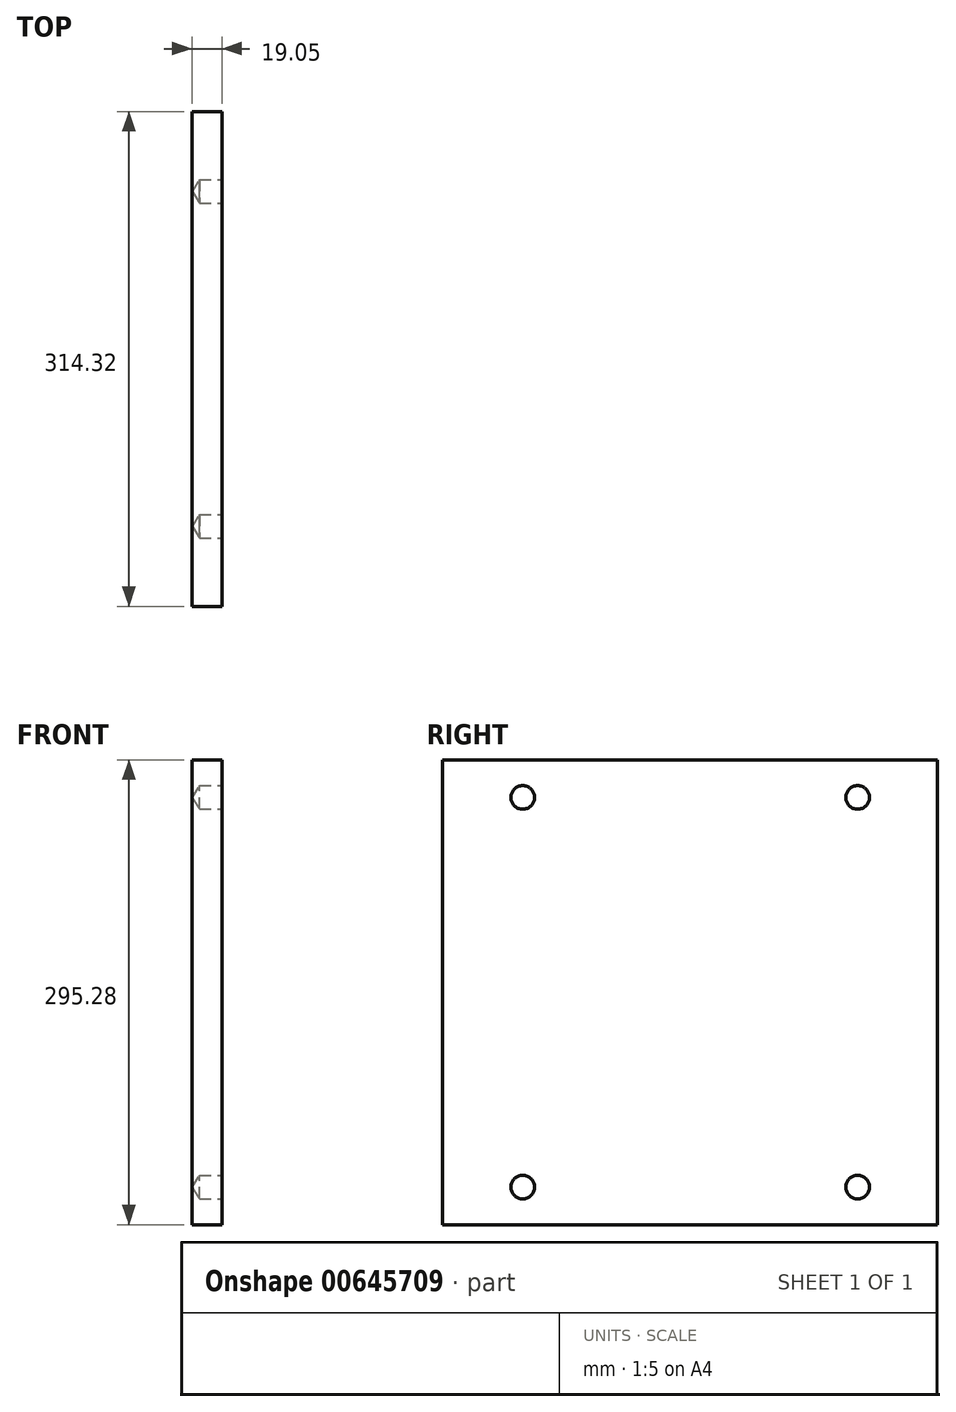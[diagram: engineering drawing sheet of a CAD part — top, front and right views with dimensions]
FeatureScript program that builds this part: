
annotation { "Feature Type Name" : "Feature", "Feature Type Description" : "" }
export const myFeature = defineFeature(function(context is Context, id is Id, definition is map)
    precondition{}
    {
        {
            var Q0;
            Q0=qCreatedBy(makeId("Right.planeOp"),FACE);
            var sketch = newSketch(context, id + "F0", { "sketchPlane" : qUnion([Q0])});
            skLineSegment(sketch, "E0.bottom", {"start": v(157.16, 147.64) * mm, "end": v(-157.16, 147.64) * mm});
            skLineSegment(sketch, "E0.top", {"start": v(157.16, -147.64) * mm, "end": v(-157.16, -147.64) * mm});
            skLineSegment(sketch, "E0.left", {"start": v(157.16, 147.64) * mm, "end": v(157.16, -147.64) * mm});
            skLineSegment(sketch, "E0.right", {"start": v(-157.16, 147.64) * mm, "end": v(-157.16, -147.64) * mm});
            skPoint(sketch, "E0.middle", {"position": v(0, 0) * mm});
            skSolve(sketch);
        }
        {
            var Q0;
            Q0=makeQuery(id+"F0.imprint","IMPRINT",FACE,{"disambiguationData":[TD([[makeQuery(id+"F0.imprint","IMPRINT",EDGE,{"derivedFrom":sQuery(id+"F0.wireOp",EDGE,"E0.bottom")}),1.0]])]});
            extrude(context, id + "F1", {"entities" : qUnion([Q0]), "depth" : 19.05 * mm, "offsetDistance" : 25.4 * mm});
        }
        {
            var Q0;
            Q0=makeQuery(id+"F1.opExtrude","CAP_FACE",FACE,{"disambiguationData":[OSD([sQuery(id+"F0.wireOp",EDGE,"E0.bottom"),sQuery(id+"F0.wireOp",EDGE,"E0.top"),sQuery(id+"F0.wireOp",EDGE,"E0.left"),sQuery(id+"F0.wireOp",EDGE,"E0.right")])],"isStart":false});
            var sketch = newSketch(context, id + "F2", { "sketchPlane" : qUnion([Q0])});
            skLineSegment(sketch, "E1", {"start": v(-157.16, 147.64) * mm, "end": v(-106.36, 147.64) * mm});
            skLineSegment(sketch, "E2", {"start": v(-106.36, 147.64) * mm, "end": v(-106.36, 123.76) * mm});
            skLineSegment(sketch, "E3", {"start": v(157.16, 147.64) * mm, "end": v(106.36, 147.64) * mm});
            skLineSegment(sketch, "E4", {"start": v(106.36, 147.64) * mm, "end": v(106.36, 123.76) * mm});
            skPoint(sketch, "E5", {"position": v(-106.36, 123.76) * mm});
            skPoint(sketch, "E6", {"position": v(106.36, 123.76) * mm});
            skLineSegment(sketch, "E7", {"start": v(-157.16, -147.64) * mm, "end": v(-106.36, -147.64) * mm});
            skLineSegment(sketch, "E8", {"start": v(-106.36, -147.64) * mm, "end": v(-106.36, -123.76) * mm});
            skLineSegment(sketch, "E9", {"start": v(157.16, -147.64) * mm, "end": v(106.36, -147.64) * mm});
            skLineSegment(sketch, "E10", {"start": v(106.36, -147.64) * mm, "end": v(106.36, -123.76) * mm});
            skPoint(sketch, "E11", {"position": v(-106.36, -123.76) * mm});
            skPoint(sketch, "E12", {"position": v(106.36, -123.76) * mm});
            skSolve(sketch);
        }
        {
            var Q0;
            Q0=sQuery(id+"F2.wireOp",VERTEX,"E5");
            var Q1;
            Q1=sQuery(id+"F2.wireOp",VERTEX,"E6");
            var Q2;
            Q2=sQuery(id+"F2.wireOp",VERTEX,"E11");
            var Q3;
            Q3=sQuery(id+"F2.wireOp",VERTEX,"E12");
            var Q4;
            Q4=makeQuery(id+"F1.opExtrude","SWEPT_BODY",BODY,{"disambiguationData":[OSD([sQuery(id+"F0.wireOp",EDGE,"E0.bottom"),sQuery(id+"F0.wireOp",EDGE,"E0.top"),sQuery(id+"F0.wireOp",EDGE,"E0.left"),sQuery(id+"F0.wireOp",EDGE,"E0.right")])]});
            hole(context, id + "F3", {"style" : HoleStyle.SIMPLE, "endStyle" : HoleEndStyle.BLIND, "holeDiameter" : 15 * mm, "majorDiameter" : 6.35 * mm, "holeDepth" : 14.22 * mm, "isTappedThrough" : true, "tappedDepth" : 12.7 * mm, "tapClearance" : 3, "startFromSketch" : true, "locations" : qUnion([Q0, Q1, Q2, Q3]), "scope" : qUnion([Q4])});
        }
    });
